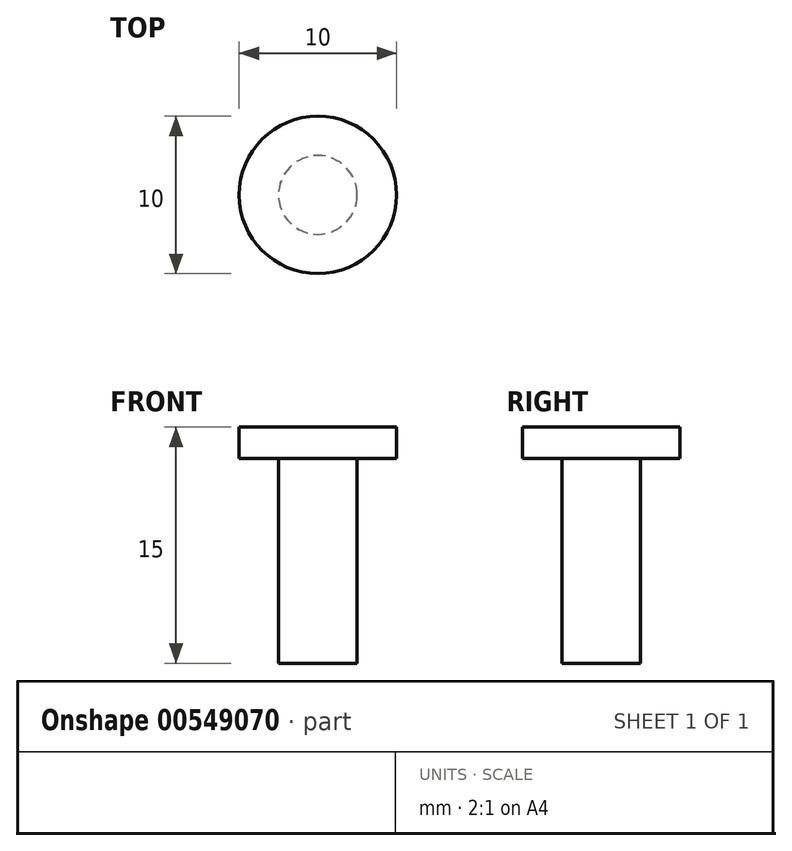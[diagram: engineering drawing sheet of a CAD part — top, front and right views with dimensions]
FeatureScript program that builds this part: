
annotation { "Feature Type Name" : "Feature", "Feature Type Description" : "" }
export const myFeature = defineFeature(function(context is Context, id is Id, definition is map)
    precondition{}
    {
        {
            var Q0;
            Q0=qCreatedBy(makeId("Top.planeOp"),FACE);
            var sketch = newSketch(context, id + "F0", { "sketchPlane" : qUnion([Q0])});
            skCircle(sketch, "E0", {"center": v(0, 0) * mm, "radius": 5 * mm});
            skSolve(sketch);
        }
        {
            var Q0;
            Q0=sQuery(id+"F0.wireOp",EDGE,"E0");
            extrude(context, id + "F1", {"bodyType" : ToolBodyType.SURFACE, "surfaceEntities" : qUnion([Q0]), "depth" : 2 * mm, "offsetDistance" : 25 * mm});
        }
        {
            var Q0;
            Q0=makeQuery(id+"F0.imprint","IMPRINT",FACE,{"disambiguationData":[TD([[makeQuery(id+"F0.imprint","IMPRINT",EDGE,{"derivedFrom":sQuery(id+"F0.wireOp",EDGE,"E0")}),1.0]])]});
            extrude(context, id + "F2", {"entities" : qUnion([Q0]), "depth" : 2 * mm, "offsetDistance" : 25 * mm});
        }
        {
            var Q0;
            Q0=qCreatedBy(makeId("Top.planeOp"),FACE);
            var sketch = newSketch(context, id + "F3", { "sketchPlane" : qUnion([Q0])});
            skCircle(sketch, "E1", {"center": v(0, 0) * mm, "radius": 2.5 * mm});
            skSolve(sketch);
        }
        {
            var Q0;
            Q0=makeQuery(id+"F3.imprint","IMPRINT",FACE,{"disambiguationData":[TD([[makeQuery(id+"F3.imprint","IMPRINT",EDGE,{"derivedFrom":sQuery(id+"F3.wireOp",EDGE,"E1")}),1.0]])]});
            extrude(context, id + "F4", {"entities" : qUnion([Q0]), "operationType" : NewBodyOperationType.ADD, "depth" : -13 * mm, "offsetDistance" : 25 * mm});
        }
        {
            var Q0;
            Q0=makeQuery(id+"F1.opExtrude","SWEPT_BODY",BODY,{"disambiguationData":[OSD([sQuery(id+"F0.wireOp",EDGE,"E0")])]});
            deleteBodies(context, id + "F5", {"entities" : qUnion([Q0])});
        }
    });
